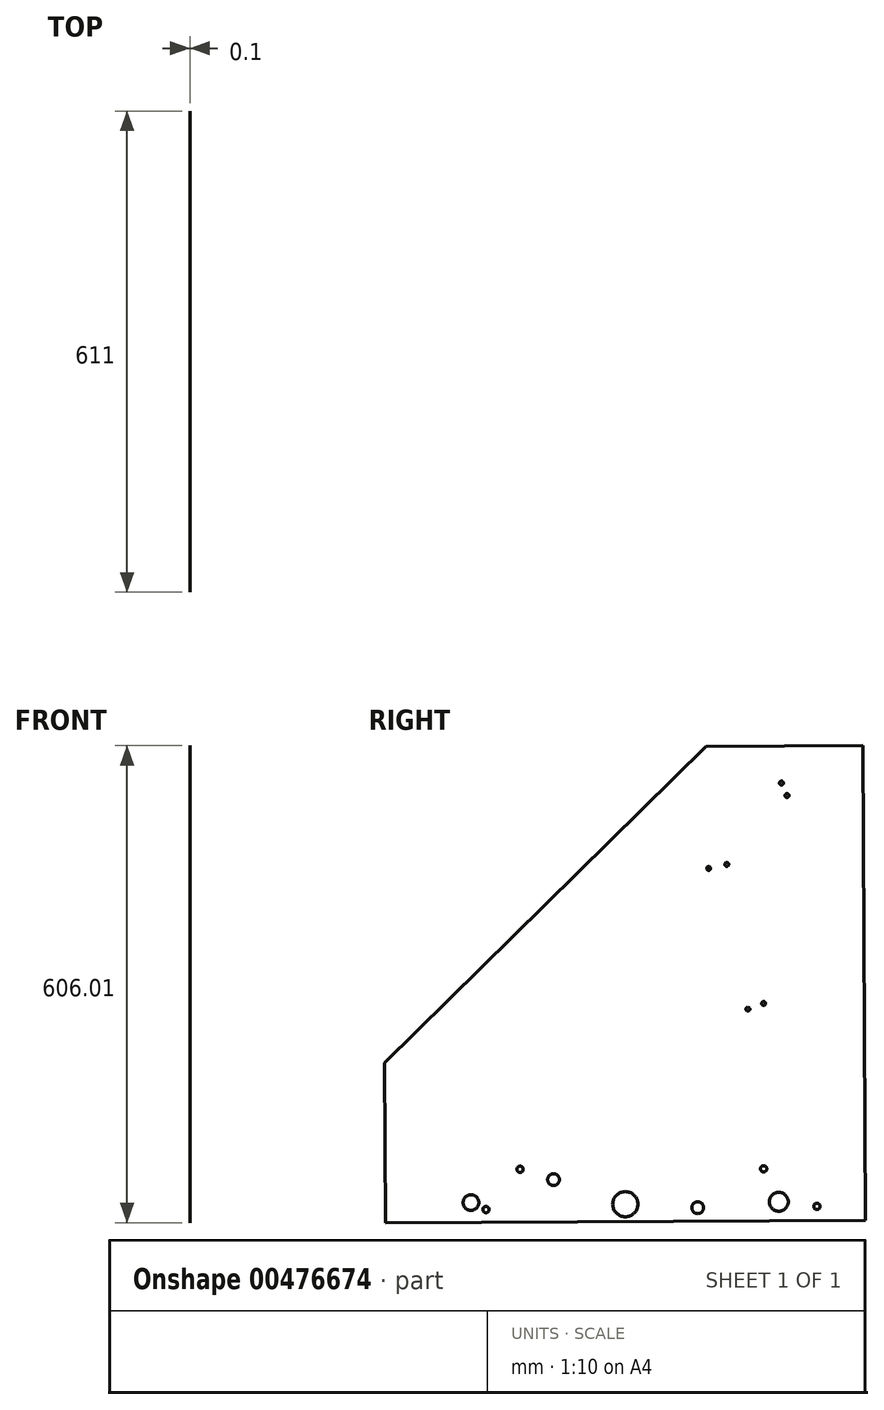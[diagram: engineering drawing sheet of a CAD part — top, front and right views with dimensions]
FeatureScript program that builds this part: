
annotation { "Feature Type Name" : "Feature", "Feature Type Description" : "" }
export const myFeature = defineFeature(function(context is Context, id is Id, definition is map)
    precondition{}
    {
        {
            var Q0;
            Q0=qCreatedBy(makeId("Right.planeOp"),FACE);
            var sketch = newSketch(context, id + "F0", { "sketchPlane" : qUnion([Q0])});
            skLineSegment(sketch, "E0.bottom", {"start": v(0, 0) * mm, "end": v(-610, -3) * mm});
            skLineSegment(sketch, "E0.left", {"start": v(0, 0) * mm, "end": v(-2.97, 603) * mm});
            skLineSegment(sketch, "E0.right", {"start": v(-610, -3) * mm, "end": v(-611, 200) * mm});
            skCircle(sketch, "E1", {"center": v(-61.7, 17.7) * mm, "radius": 4 * mm});
            skCircle(sketch, "E2", {"center": v(-110.12, 23.46) * mm, "radius": 12 * mm});
            skCircle(sketch, "E3", {"center": v(-129.32, 65.36) * mm, "radius": 4 * mm});
            skCircle(sketch, "E4", {"center": v(-213.08, 15.95) * mm, "radius": 7.5 * mm});
            skCircle(sketch, "E5", {"center": v(-305.1, 20.5) * mm, "radius": 16 * mm});
            skCircle(sketch, "E6", {"center": v(-396.26, 51.63) * mm, "radius": 7.5 * mm});
            skCircle(sketch, "E7", {"center": v(-482.07, 13.62) * mm, "radius": 4 * mm});
            skCircle(sketch, "E8", {"center": v(-438.73, 64.84) * mm, "radius": 4 * mm});
            skCircle(sketch, "E9", {"center": v(-501.12, 22.53) * mm, "radius": 10 * mm});
            skLineSegment(sketch, "E10", {"start": v(-611, 200) * mm, "end": v(-202.97, 602.01) * mm});
            skLineSegment(sketch, "E11", {"start": v(-2.97, 603) * mm, "end": v(-202.97, 602.01) * mm});
            skCircle(sketch, "E12", {"center": v(-149.32, 268.27) * mm, "radius": 2.5 * mm});
            skCircle(sketch, "E13", {"center": v(-129.36, 275.37) * mm, "radius": 2.5 * mm});
            skCircle(sketch, "E14", {"center": v(-199.2, 447.02) * mm, "radius": 2.5 * mm});
            skCircle(sketch, "E15", {"center": v(-176.23, 452.14) * mm, "radius": 2.5 * mm});
            skCircle(sketch, "E16", {"center": v(-106.74, 555.48) * mm, "radius": 2.5 * mm});
            skCircle(sketch, "E17", {"center": v(-99.66, 539.52) * mm, "radius": 2.5 * mm});
            skSolve(sketch);
        }
        {
            var Q0;
            Q0=makeQuery(id+"F0.imprint","IMPRINT",FACE,{"disambiguationData":[TD([[makeQuery(id+"F0.imprint","IMPRINT",EDGE,{"derivedFrom":sQuery(id+"F0.wireOp",EDGE,"E0.bottom")}),-1.0]])]});
            extrude(context, id + "F1", {"entities" : qUnion([Q0]), "depth" : 0.1 * mm});
        }
    });
